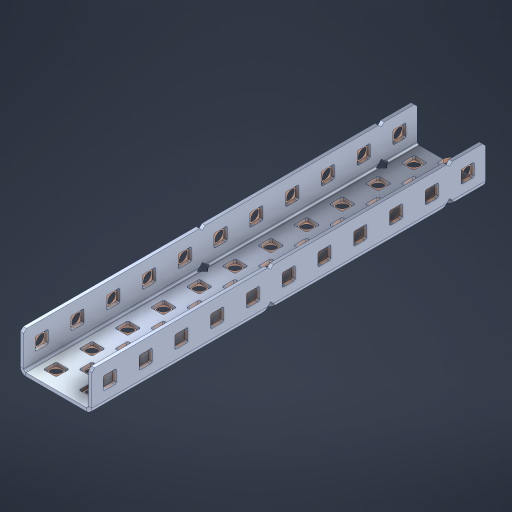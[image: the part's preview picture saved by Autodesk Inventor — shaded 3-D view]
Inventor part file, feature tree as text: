
AUTODESK INVENTOR PART (.ipt)
format: ipt  version: 2023 (Build 270158000, 158)  size: 988,160 bytes
history: native  units: in
note: dims shown in document units (in); Inventor stores cm internally (conversion verified against a paired STEP export)
features: other x62, extrude x53, sheet_metal_op x11, sketch x10, pattern_linear x2, mirror x1, chamfer x1
ambient origin geometry x8: Origin, YZ Plane, XZ Plane, XY Plane, X Axis, Y Axis, Z Axis, Center Point
bodies: Solid1 (feature_tree), Body (feature_tree)
feature tree (140):
  sheet_metal_op  "Flanges"
  other  "Flange Pattern Plane"
  other  "Flange Pattern Sketch"
  sheet_metal_op  "Flange Pattern"
  sheet_metal_op  "Body Pattern"
  pattern_linear  "Center Pattern"  Spacing1=0.0469in  [1 undecoded]
  other  "Arc Length"
  mirror  "Notch Mirror"
  pattern_linear  "Notch Pattern"  Spacing1=0.182in  [1 undecoded]
  chamfer  "End Chamfer"
  extrude  "Half Cut"  Depth=0.02in
  sketch  "Sketch1"  dims[d0=1.0in]
  other  "Plate1"
  sketch  "Sketch2"  dims[d1=5.5in]
  other  "Plate2"
  sheet_metal_op  "Bend1"
  sheet_metal_op  "Corner1"
  sketch  "Sketch3"  dims[d2=0.0469in]
  sketch  "Sketch7"  dims[d3=0.0469in]
  other  "Srf1"
  other  "Srf2"
  sketch  "Sketch8"  dims[d4=0.0234in]
  sketch  "Sketch9"  dims[d5=0.0938in]
  other  "Srf91"
  sheet_metal_op  "Body Pattern Sketch"
  other  "Srf92"
  sketch  "Sketch13"  dims[d6=0.0469in]
  sketch  "Sketch14"  dims[d7=0.5in d8=90.0deg d9=0.0312in]
  sketch  "Sketch15"  dims[d10=0.1875in]
  sketch  "Sketch16"  dims[d11=0.0469in d12=0.0469in d16=0.182in d17=0.02in d18=0.0469in d19=0.0in d20=0.25in d21=0.25in d38=4.3307in d40=0.5in d41=0.7874in d43=1.0in d46=0.172in d47=1.0in d48=0.0in d49=0.182in d50=0.02in d51=0.25in d52=0.25in d53=0.0469in d54=0.0in d55=0.172in d56=1.0in d57=0.0in d58=0.25in d60=4.3307in d62=0.5in d63=0.7874in d65=0.5in d85=0.1227in d86=0.1659in d88=0.04in d89=0.0469in d90=0.0in d91=0.04in d92=0.0491in d95=2.5in d96=0.04in d97=0.25in d98=45.0deg d99=0.25in d100=0.5in d101=0.0in d102=2.497in d106=0.182in d107=0.02in d108=0.5in d109=0.5in d110=0.0469in d111=0.0in d112=0.172in d113=0.5in d114=0.0in d117=0.5in d118=0.5in d119=0.5in]
  other  "Srf786"
  other  "Srf823"
  other  "Srf824"
  other  "Srf825"
  other  "Srf826"
  other  "Srf827"
  other  "Srf828"
  other  "Srf829"
  other  "Srf856"
  other  "Srf857"
  other  "Srf858"
  other  "Srf859"
  other  "Srf860"
  other  "Srf861"
  other  "Srf862"
  other  "Srf889"
  other  "Srf890"
  other  "Srf891"
  other  "Srf892"
  other  "Srf893"
  other  "Srf894"
  other  "Srf895"
  other  "Srf896"
  other  "Srf922"
  other  "Srf923"
  other  "Srf924"
  other  "Srf925"
  other  "Srf926"
  other  "Srf959"
  other  "Srf960"
  other  "Srf961"
  other  "Srf962"
  other  "Srf963"
  other  "Srf996"
  other  "Srf997"
  other  "Srf1143"
  other  "Srf1144"
  other  "Srf1145"
  other  "Srf1146"
  other  "Srf1147"
  other  "Srf1148"
  other  "Srf1149"
  other  "Srf1150"
  other  "Srf1199"
  other  "Srf1200"
  other  "Srf1201"
  other  "Srf1202"
  other  "Srf1203"
  other  "Srf1204"
  other  "Srf1205"
  other  "Srf1206"
  sheet_metal_op  "Flange Stamp"
  sheet_metal_op  "Flange Circle"
  sheet_metal_op  "Body Stamp"
  sheet_metal_op  "Body Circle"
  other  "Center Stamp"
  other  "Center Circle"
  sheet_metal_op  "Notch"
  extrude  "ExtrusionSrf2"  Depth=0.0469in
  extrude  "ExtrusionSrf92"  TaperAngle=0.0deg  [1 undecoded]
  extrude  "ExtrusionSrf823"  Depth=0.5in
  extrude  "ExtrusionSrf824"  Depth=0.5in
  extrude  "ExtrusionSrf825"  Depth=0.5in
  extrude  "ExtrusionSrf826"  Depth=0.5in
  extrude  "ExtrusionSrf827"  Depth=1.0in TaperAngle=0.0deg
  extrude  "ExtrusionSrf828"  Depth=0.5in
  extrude  "ExtrusionSrf829"  Depth=0.02in
  extrude  "ExtrusionSrf856"  Depth=0.5in
  extrude  "ExtrusionSrf857"  Depth=0.5in
  extrude  "ExtrusionSrf858"  Depth=0.0469in
  extrude  "ExtrusionSrf859"  TaperAngle=0.0deg  [1 undecoded]
  extrude  "ExtrusionSrf860"  Depth=0.5in
  extrude  "ExtrusionSrf861"  Depth=1.0in TaperAngle=0.0deg
  extrude  "ExtrusionSrf862"  Depth=0.5in
  extrude  "ExtrusionSrf889"  Depth=0.5in
  extrude  "ExtrusionSrf890"  Depth=0.5in
  extrude  "ExtrusionSrf891"  Depth=0.5in
  extrude  "ExtrusionSrf892"  Depth=0.5in
  extrude  "ExtrusionSrf893"  Depth=0.5in
  extrude  "ExtrusionSrf894"  Depth=0.0469in
  extrude  "ExtrusionSrf895"  TaperAngle=0.0deg  [1 undecoded]
  extrude  "ExtrusionSrf896"  Depth=0.5in
  extrude  "ExtrusionSrf922"  Depth=0.5in
  extrude  "ExtrusionSrf923"  Depth=2.5in
  extrude  "ExtrusionSrf924"  Depth=0.5in TaperAngle=45.0deg
  extrude  "ExtrusionSrf925"  Depth=0.5in
  extrude  "ExtrusionSrf926"  Depth=0.5in TaperAngle=0.0deg
  extrude  "ExtrusionSrf959"  Depth=0.5in
  extrude  "ExtrusionSrf960"  Depth=0.5in
  extrude  "ExtrusionSrf961"  Depth=0.02in
  extrude  "ExtrusionSrf962"  Depth=0.5in
  extrude  "ExtrusionSrf963"  Depth=0.5in
  extrude  "ExtrusionSrf996"  Depth=0.0469in
  extrude  "ExtrusionSrf997"  TaperAngle=0.0deg  [1 undecoded]
  extrude  "ExtrusionSrf1143"  Depth=0.5in
  extrude  "ExtrusionSrf1144"  Depth=0.5in TaperAngle=0.0deg
  extrude  "ExtrusionSrf1145"  Depth=0.5in
  extrude  "ExtrusionSrf1146"  Depth=0.5in
  extrude  "ExtrusionSrf1147"  Depth=0.5in
  extrude  "ExtrusionSrf1148"  [1 undecoded]
  extrude  "ExtrusionSrf1149"  [1 undecoded]
  extrude  "ExtrusionSrf1150"  [1 undecoded]
  extrude  "ExtrusionSrf1199"  [1 undecoded]
  extrude  "ExtrusionSrf1200"  [1 undecoded]
  extrude  "ExtrusionSrf1201"  [1 undecoded]
  extrude  "ExtrusionSrf1202"  [1 undecoded]
  extrude  "ExtrusionSrf1203"  [1 undecoded]
  extrude  "ExtrusionSrf1204"  [1 undecoded]
  extrude  "ExtrusionSrf1205"  [1 undecoded]
  extrude  "ExtrusionSrf1206"  [1 undecoded]
note: 17 required parameter values undecoded (feature->parameter linkage not recoverable at this tier; creation-order binding heuristic only, values carry confidence <= 0.55)
